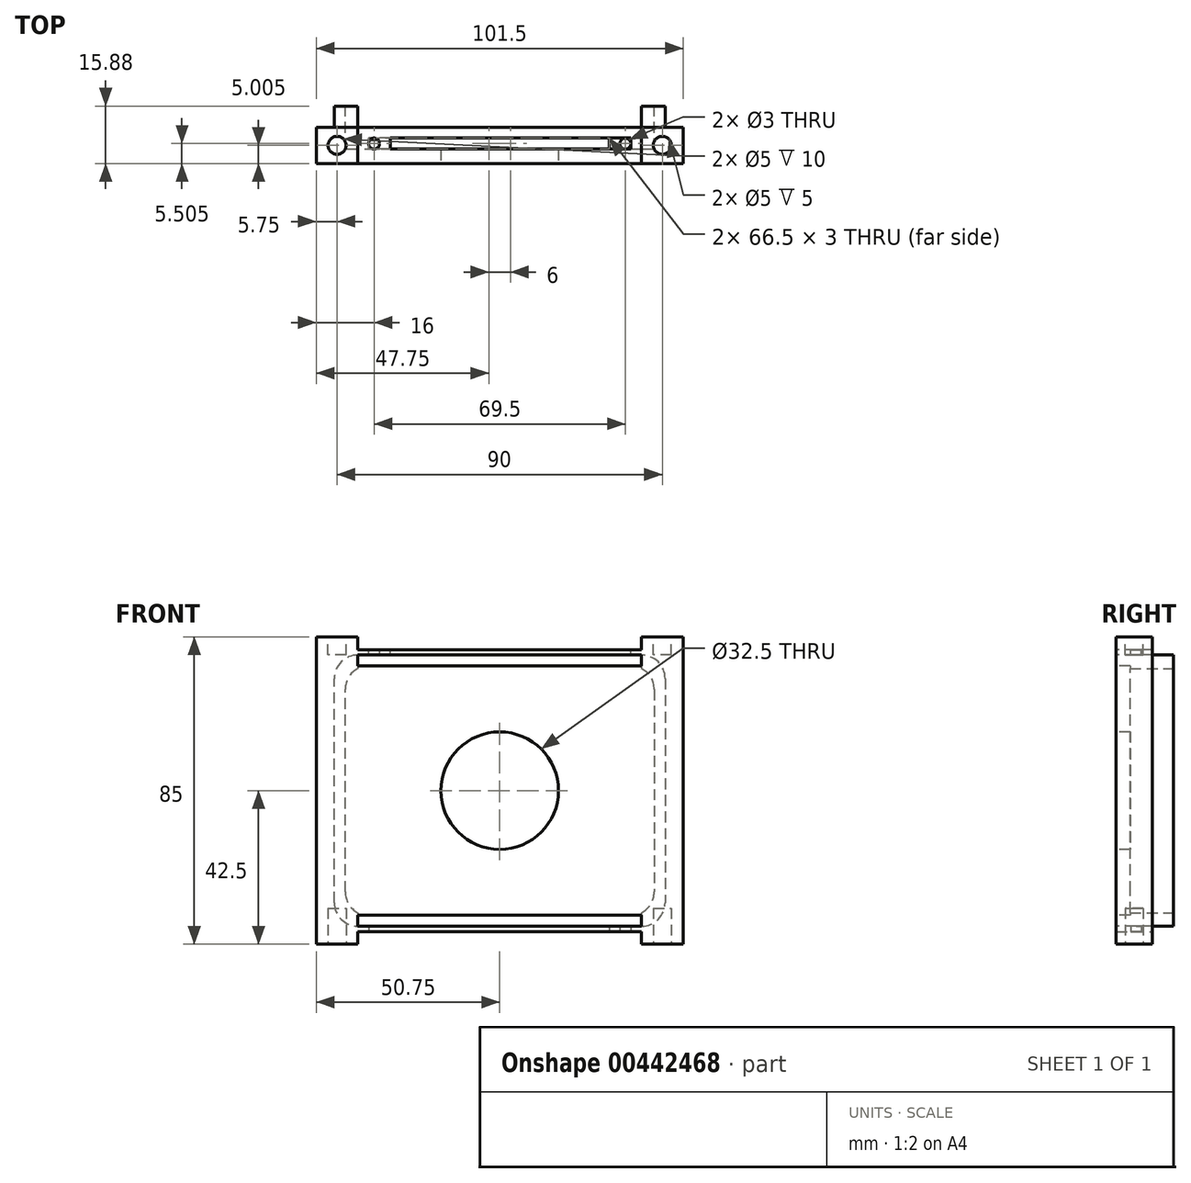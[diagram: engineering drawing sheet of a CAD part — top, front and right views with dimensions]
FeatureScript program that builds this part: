
annotation { "Feature Type Name" : "Feature", "Feature Type Description" : "" }
export const myFeature = defineFeature(function(context is Context, id is Id, definition is map)
    precondition{}
    {
        {
            var Q0;
            Q0=qCreatedBy(makeId("Front.planeOp"),FACE);
            var sketch = newSketch(context, id + "F0", { "sketchPlane" : qUnion([Q0])});
            skLineSegment(sketch, "E0.bottom", {"start": v(50.75, 42.5) * mm, "end": v(-50.75, 42.5) * mm});
            skLineSegment(sketch, "E0.top", {"start": v(50.75, -42.5) * mm, "end": v(-50.75, -42.5) * mm});
            skLineSegment(sketch, "E0.left", {"start": v(50.75, 42.5) * mm, "end": v(50.75, -42.5) * mm});
            skLineSegment(sketch, "E0.right", {"start": v(-50.75, 42.5) * mm, "end": v(-50.75, -42.5) * mm});
            skPoint(sketch, "E0.middle", {"position": v(0, 0) * mm});
            skSolve(sketch);
        }
        {
            var Q0;
            Q0 = qSketchRegion(id + "F0", true);
            extrude(context, id + "F1", {"entities" : qUnion([Q0]), "depth" : 15.88 * mm});
        }
        {
            var Q0;
            Q0=makeQuery(id+"F1.opExtrude","CAP_FACE",FACE,{"disambiguationData":[OSD([sQuery(id+"F0.wireOp",EDGE,"E0.bottom"),sQuery(id+"F0.wireOp",EDGE,"E0.top"),sQuery(id+"F0.wireOp",EDGE,"E0.left"),sQuery(id+"F0.wireOp",EDGE,"E0.right")])],"isStart":false});
            var sketch = newSketch(context, id + "F2", { "sketchPlane" : qUnion([Q0])});
            skCircle(sketch, "E1", {"center": v(0, 0) * mm, "radius": 16.25 * mm});
            skSolve(sketch);
        }
        {
            var Q0;
            Q0 = qSketchRegion(id + "F2", true);
            extrude(context, id + "F3", {"entities" : qUnion([Q0]), "operationType" : NewBodyOperationType.REMOVE, "oppositeDirection" : true, "depth" : 25 * mm});
        }
        {
            var Q0;
            Q0=makeQuery(id+"F1.opExtrude","CAP_FACE",FACE,{"disambiguationData":[OSD([sQuery(id+"F0.wireOp",EDGE,"E0.bottom"),sQuery(id+"F0.wireOp",EDGE,"E0.top"),sQuery(id+"F0.wireOp",EDGE,"E0.left"),sQuery(id+"F0.wireOp",EDGE,"E0.right")])],"isStart":true});
            var sketch = newSketch(context, id + "F4", { "sketchPlane" : qUnion([Q0])});
            skLineSegment(sketch, "E2.bottom", {"start": v(45.75, 37.5) * mm, "end": v(-45.75, 37.5) * mm, "construction": true});
            skLineSegment(sketch, "E2.top", {"start": v(45.75, -37.5) * mm, "end": v(-45.75, -37.5) * mm, "construction": true});
            skLineSegment(sketch, "E2.left", {"start": v(45.75, 37.5) * mm, "end": v(45.75, -37.5) * mm, "construction": true});
            skLineSegment(sketch, "E2.right", {"start": v(-45.75, 37.5) * mm, "end": v(-45.75, -37.5) * mm, "construction": true});
            skPoint(sketch, "E2.middle", {"position": v(0, 0) * mm});
            skCircle(sketch, "E3", {"center": v(-39.25, 31) * mm, "radius": 6.5 * mm, "construction": true});
            skCircle(sketch, "E4", {"center": v(-39.25, -31) * mm, "radius": 6.5 * mm, "construction": true});
            skCircle(sketch, "E5", {"center": v(39.25, -31) * mm, "radius": 6.5 * mm, "construction": true});
            skCircle(sketch, "E6", {"center": v(39.25, 31) * mm, "radius": 6.5 * mm, "construction": true});
            skLineSegment(sketch, "E7", {"start": v(-45.75, 31) * mm, "end": v(-45.75, -31) * mm});
            skLineSegment(sketch, "E8", {"start": v(-39.25, -37.5) * mm, "end": v(39.25, -37.5) * mm});
            skLineSegment(sketch, "E9", {"start": v(45.75, -31) * mm, "end": v(45.75, 31) * mm});
            skLineSegment(sketch, "E10", {"start": v(39.25, 37.5) * mm, "end": v(-39.25, 37.5) * mm});
            skArc(sketch, "E11", {"start": v(-39.25, 37.5) * mm, "mid": v(-43.85, 35.6) * mm, "end": v(-45.75, 31) * mm});
            skArc(sketch, "E12", {"start": v(-45.75, -31) * mm, "mid": v(-43.85, -35.6) * mm, "end": v(-39.25, -37.5) * mm});
            skArc(sketch, "E13", {"start": v(39.25, -37.5) * mm, "mid": v(43.85, -35.6) * mm, "end": v(45.75, -31) * mm});
            skArc(sketch, "E14", {"start": v(45.75, 31) * mm, "mid": v(43.85, 35.6) * mm, "end": v(39.25, 37.5) * mm});
            skLineSegment(sketch, "E15.bottom", {"start": v(50.75, 42.5) * mm, "end": v(-50.75, 42.5) * mm});
            skLineSegment(sketch, "E15.top", {"start": v(50.75, -42.5) * mm, "end": v(-50.75, -42.5) * mm});
            skLineSegment(sketch, "E15.left", {"start": v(50.75, 42.5) * mm, "end": v(50.75, -42.5) * mm});
            skLineSegment(sketch, "E15.right", {"start": v(-50.75, 42.5) * mm, "end": v(-50.75, -42.5) * mm});
            skSolve(sketch);
        }
        {
            var Q0;
            Q0 = qSketchRegion(id + "F4", true);
            extrude(context, id + "F5", {"entities" : qUnion([Q0]), "operationType" : NewBodyOperationType.REMOVE, "oppositeDirection" : true, "depth" : 5.88 * mm});
        }
        {
            var Q0;
            Q0=makeQuery(id+"F1.opExtrude","CAP_FACE",FACE,{"disambiguationData":[OSD([sQuery(id+"F0.wireOp",EDGE,"E0.bottom"),sQuery(id+"F0.wireOp",EDGE,"E0.top"),sQuery(id+"F0.wireOp",EDGE,"E0.left"),sQuery(id+"F0.wireOp",EDGE,"E0.right")])],"isStart":true});
            var sketch = newSketch(context, id + "F6", { "sketchPlane" : qUnion([Q0])});
            skLineSegment(sketch, "E16.bottom", {"start": v(42.75, 34.5) * mm, "end": v(-42.75, 34.5) * mm, "construction": true});
            skLineSegment(sketch, "E16.top", {"start": v(42.75, -34.5) * mm, "end": v(-42.75, -34.5) * mm, "construction": true});
            skLineSegment(sketch, "E16.left", {"start": v(42.75, 34.5) * mm, "end": v(42.75, -34.5) * mm, "construction": true});
            skLineSegment(sketch, "E16.right", {"start": v(-42.75, 34.5) * mm, "end": v(-42.75, -34.5) * mm, "construction": true});
            skPoint(sketch, "E16.middle", {"position": v(0, 0) * mm});
            skCircle(sketch, "E17", {"center": v(-36.25, 28) * mm, "radius": 6.5 * mm, "construction": true});
            skCircle(sketch, "E18", {"center": v(-36.25, -28) * mm, "radius": 6.5 * mm, "construction": true});
            skCircle(sketch, "E19", {"center": v(36.25, -28) * mm, "radius": 6.5 * mm, "construction": true});
            skCircle(sketch, "E20", {"center": v(36.25, 28) * mm, "radius": 6.5 * mm, "construction": true});
            skLineSegment(sketch, "E21", {"start": v(-42.75, 28) * mm, "end": v(-42.75, -28) * mm});
            skLineSegment(sketch, "E22", {"start": v(-36.25, -34.5) * mm, "end": v(36.25, -34.5) * mm});
            skLineSegment(sketch, "E23", {"start": v(42.75, -28) * mm, "end": v(42.75, 28) * mm});
            skLineSegment(sketch, "E24", {"start": v(36.25, 34.5) * mm, "end": v(-36.25, 34.5) * mm});
            skArc(sketch, "E25", {"start": v(-36.25, 34.5) * mm, "mid": v(-40.85, 32.6) * mm, "end": v(-42.75, 28) * mm});
            skArc(sketch, "E26", {"start": v(-42.75, -28) * mm, "mid": v(-40.85, -32.6) * mm, "end": v(-36.25, -34.5) * mm});
            skArc(sketch, "E27", {"start": v(36.25, -34.5) * mm, "mid": v(40.85, -32.6) * mm, "end": v(42.75, -28) * mm});
            skArc(sketch, "E28", {"start": v(42.75, 28) * mm, "mid": v(40.85, 32.6) * mm, "end": v(36.25, 34.5) * mm});
            skSolve(sketch);
        }
        {
            var Q0;
            Q0 = qSketchRegion(id + "F6", true);
            extrude(context, id + "F7", {"entities" : qUnion([Q0]), "operationType" : NewBodyOperationType.REMOVE, "oppositeDirection" : true, "depth" : 12 * mm});
        }
        {
            var Q0;
            Q0=makeQuery(id+"F1.opExtrude","SWEPT_FACE",FACE,{"disambiguationData":[OSD([sQuery(id+"F0.wireOp",EDGE,"E0.bottom")])]});
            var sketch = newSketch(context, id + "F8", { "sketchPlane" : qUnion([Q0])});
            skLineSegment(sketch, "E29.bottom", {"start": v(-39.25, -5.88) * mm, "end": v(39.25, -5.88) * mm});
            skLineSegment(sketch, "E29.top", {"start": v(-39.25, -15.88) * mm, "end": v(39.25, -15.88) * mm});
            skLineSegment(sketch, "E29.left", {"start": v(-39.25, -5.88) * mm, "end": v(-39.25, -15.88) * mm});
            skLineSegment(sketch, "E29.right", {"start": v(39.25, -5.88) * mm, "end": v(39.25, -15.88) * mm});
            skSolve(sketch);
        }
        {
            var Q0;
            Q0 = qSketchRegion(id + "F8", true);
            extrude(context, id + "F9", {"entities" : qUnion([Q0]), "operationType" : NewBodyOperationType.REMOVE, "oppositeDirection" : true, "depth" : 3.5 * mm});
        }
        {
            var Q0;
            Q0=makeQuery(id+"F1.opExtrude","SWEPT_FACE",FACE,{"disambiguationData":[OSD([sQuery(id+"F0.wireOp",EDGE,"E0.top")])]});
            var sketch = newSketch(context, id + "F10", { "sketchPlane" : qUnion([Q0])});
            skLineSegment(sketch, "E30.bottom", {"start": v(-39.25, 15.88) * mm, "end": v(39.25, 15.88) * mm});
            skLineSegment(sketch, "E30.top", {"start": v(-39.25, 5.88) * mm, "end": v(39.25, 5.88) * mm});
            skLineSegment(sketch, "E30.left", {"start": v(-39.25, 15.88) * mm, "end": v(-39.25, 5.88) * mm});
            skLineSegment(sketch, "E30.right", {"start": v(39.25, 15.88) * mm, "end": v(39.25, 5.88) * mm});
            skSolve(sketch);
        }
        {
            var Q0;
            Q0 = qSketchRegion(id + "F10", true);
            extrude(context, id + "F11", {"entities" : qUnion([Q0]), "operationType" : NewBodyOperationType.REMOVE, "oppositeDirection" : true, "depth" : 3.5 * mm});
        }
        {
            var Q0;
            Q0=makeQuery(id+"F1.opExtrude","CAP_FACE",FACE,{"disambiguationData":[OSD([sQuery(id+"F0.wireOp",EDGE,"E0.bottom"),sQuery(id+"F0.wireOp",EDGE,"E0.top"),sQuery(id+"F0.wireOp",EDGE,"E0.left"),sQuery(id+"F0.wireOp",EDGE,"E0.right")])],"isStart":false});
            var sketch = newSketch(context, id + "F12", { "sketchPlane" : qUnion([Q0])});
            skLineSegment(sketch, "E31.bottom", {"start": v(-39.25, 37.5) * mm, "end": v(39.25, 37.5) * mm});
            skLineSegment(sketch, "E31.top", {"start": v(-39.25, 34.5) * mm, "end": v(39.25, 34.5) * mm});
            skLineSegment(sketch, "E31.left", {"start": v(-39.25, 37.5) * mm, "end": v(-39.25, 34.5) * mm});
            skLineSegment(sketch, "E31.right", {"start": v(39.25, 37.5) * mm, "end": v(39.25, 34.5) * mm});
            skLineSegment(sketch, "E32.bottom", {"start": v(39.25, -37.5) * mm, "end": v(-39.25, -37.5) * mm});
            skLineSegment(sketch, "E32.top", {"start": v(39.25, -34.5) * mm, "end": v(-39.25, -34.5) * mm});
            skLineSegment(sketch, "E32.left", {"start": v(39.25, -37.5) * mm, "end": v(39.25, -34.5) * mm});
            skLineSegment(sketch, "E32.right", {"start": v(-39.25, -37.5) * mm, "end": v(-39.25, -34.5) * mm});
            skSolve(sketch);
        }
        {
            var Q0;
            Q0 = qSketchRegion(id + "F12", true);
            extrude(context, id + "F13", {"entities" : qUnion([Q0]), "operationType" : NewBodyOperationType.REMOVE, "oppositeDirection" : true, "depth" : 25 * mm});
        }
        {
            var Q0;
            Q0=makeQuery(id+"F9.boolean.opBoolean","COPY",FACE,{"derivedFrom":makeQuery(id+"F9.opExtrude","CAP_FACE",FACE,{"disambiguationData":[OSD([sQuery(id+"F8.wireOp",EDGE,"E29.bottom"),sQuery(id+"F8.wireOp",EDGE,"E29.top"),sQuery(id+"F8.wireOp",EDGE,"E29.left"),sQuery(id+"F8.wireOp",EDGE,"E29.right")])],"isStart":false})});
            var sketch = newSketch(context, id + "F14", { "sketchPlane" : qUnion([Q0])});
            skLineSegment(sketch, "E33.bottom", {"start": v(-39.25, -5.88) * mm, "end": v(39.25, -5.88) * mm});
            skLineSegment(sketch, "E33.top", {"start": v(-39.25, 11.7) * mm, "end": v(39.25, 11.7) * mm});
            skLineSegment(sketch, "E33.left", {"start": v(-39.25, -5.88) * mm, "end": v(-39.25, 11.7) * mm});
            skLineSegment(sketch, "E33.right", {"start": v(39.25, -5.88) * mm, "end": v(39.25, 11.7) * mm});
            skSolve(sketch);
        }
        {
            var Q0;
            Q0 = qSketchRegion(id + "F14", true);
            extrude(context, id + "F15", {"entities" : qUnion([Q0]), "operationType" : NewBodyOperationType.REMOVE, "oppositeDirection" : true, "depth" : 200 * mm});
        }
        {
            var Q0;
            Q0=makeQuery(id+"F5.boolean.opBoolean","COPY",FACE,{"derivedFrom":makeQuery(id+"F5.opExtrude","CAP_FACE",FACE,{"disambiguationData":[OSD([sQuery(id+"F4.wireOp",EDGE,"E7"),sQuery(id+"F4.wireOp",EDGE,"E8"),sQuery(id+"F4.wireOp",EDGE,"E9"),sQuery(id+"F4.wireOp",EDGE,"E10"),sQuery(id+"F4.wireOp",EDGE,"E11"),sQuery(id+"F4.wireOp",EDGE,"E12"),sQuery(id+"F4.wireOp",EDGE,"E13"),sQuery(id+"F4.wireOp",EDGE,"E14"),sQuery(id+"F4.wireOp",EDGE,"E15.bottom"),sQuery(id+"F4.wireOp",EDGE,"E15.top"),sQuery(id+"F4.wireOp",EDGE,"E15.left"),sQuery(id+"F4.wireOp",EDGE,"E15.right")])],"isStart":false})});
            var sketch = newSketch(context, id + "F16", { "sketchPlane" : qUnion([Q0])});
            skLineSegment(sketch, "E34.bottom", {"start": v(-39.25, 37.5) * mm, "end": v(39.25, 37.5) * mm});
            skLineSegment(sketch, "E34.top", {"start": v(-39.25, -37.5) * mm, "end": v(39.25, -37.5) * mm});
            skLineSegment(sketch, "E34.left", {"start": v(-39.25, 37.5) * mm, "end": v(-39.25, -37.5) * mm});
            skLineSegment(sketch, "E34.right", {"start": v(39.25, 37.5) * mm, "end": v(39.25, -37.5) * mm});
            skSolve(sketch);
        }
        {
            var Q0;
            Q0 = qSketchRegion(id + "F16", true);
            extrude(context, id + "F17", {"entities" : qUnion([Q0]), "operationType" : NewBodyOperationType.REMOVE, "oppositeDirection" : true, "depth" : 6.12 * mm});
        }
        {
            var Q0;
            Q0=makeQuery(id+"F9.boolean.opBoolean","COPY",FACE,{"derivedFrom":makeQuery(id+"F9.opExtrude","CAP_FACE",FACE,{"disambiguationData":[OSD([sQuery(id+"F8.wireOp",EDGE,"E29.bottom"),sQuery(id+"F8.wireOp",EDGE,"E29.top"),sQuery(id+"F8.wireOp",EDGE,"E29.left"),sQuery(id+"F8.wireOp",EDGE,"E29.right")])],"isStart":false})});
            var sketch = newSketch(context, id + "F18", { "sketchPlane" : qUnion([Q0])});
            skCircle(sketch, "E35", {"center": v(-34.75, -10.38) * mm, "radius": 1.5 * mm});
            skLineSegment(sketch, "E36.bottom", {"start": v(-30.25, -8.88) * mm, "end": v(36.25, -8.87) * mm});
            skLineSegment(sketch, "E36.top", {"start": v(-30.25, -11.88) * mm, "end": v(36.25, -11.87) * mm});
            skLineSegment(sketch, "E36.left", {"start": v(-30.25, -8.88) * mm, "end": v(-30.25, -11.88) * mm});
            skLineSegment(sketch, "E36.right", {"start": v(36.25, -8.87) * mm, "end": v(36.25, -11.87) * mm});
            skSolve(sketch);
        }
        {
            var Q0;
            Q0 = qSketchRegion(id + "F18", true);
            extrude(context, id + "F19", {"entities" : qUnion([Q0]), "operationType" : NewBodyOperationType.REMOVE, "oppositeDirection" : true, "depth" : 2 * mm});
        }
        {
            var Q0;
            Q0=makeQuery(id+"F11.boolean.opBoolean","COPY",FACE,{"derivedFrom":makeQuery(id+"F11.opExtrude","CAP_FACE",FACE,{"disambiguationData":[OSD([sQuery(id+"F10.wireOp",EDGE,"E30.bottom"),sQuery(id+"F10.wireOp",EDGE,"E30.top"),sQuery(id+"F10.wireOp",EDGE,"E30.left"),sQuery(id+"F10.wireOp",EDGE,"E30.right")])],"isStart":false})});
            var sketch = newSketch(context, id + "F20", { "sketchPlane" : qUnion([Q0])});
            skCircle(sketch, "E37", {"center": v(34.75, 10.38) * mm, "radius": 1.5 * mm});
            skLineSegment(sketch, "E38.bottom", {"start": v(-36.25, 11.87) * mm, "end": v(30.25, 11.88) * mm});
            skLineSegment(sketch, "E38.top", {"start": v(-36.25, 8.87) * mm, "end": v(30.25, 8.88) * mm});
            skLineSegment(sketch, "E38.left", {"start": v(-36.25, 11.88) * mm, "end": v(-36.25, 8.87) * mm});
            skLineSegment(sketch, "E38.right", {"start": v(30.25, 11.88) * mm, "end": v(30.25, 8.88) * mm});
            skSolve(sketch);
        }
        {
            var Q0;
            Q0 = qSketchRegion(id + "F20", true);
            extrude(context, id + "F21", {"entities" : qUnion([Q0]), "operationType" : NewBodyOperationType.REMOVE, "oppositeDirection" : true, "depth" : 2 * mm});
        }
        {
            var Q0;
            {var subQ0=sQuery(id+"F0.wireOp",EDGE,"E0.right");var subQ1=sQuery(id+"F0.wireOp",EDGE,"E0.top");Q0=makeQuery(id+"F11.boolean.opBoolean","SPLIT",FACE,{"disambiguationData":[TD([makeQuery(id+"F1.opExtrude","SWEPT_FACE",FACE,{"disambiguationData":[OSD([subQ0])]})])],"derivedFrom":makeQuery(id+"F1.opExtrude","SWEPT_FACE",FACE,{"disambiguationData":[OSD([subQ1])]})});}
            var sketch = newSketch(context, id + "F22", { "sketchPlane" : qUnion([Q0])});
            skLineSegment(sketch, "E39", {"start": v(-50.75, 15.87) * mm, "end": v(-39.25, 5.87) * mm, "construction": true});
            skLineSegment(sketch, "E40", {"start": v(-39.25, 5.88) * mm, "end": v(50.77, 5.88) * mm, "construction": true});
            skLineSegment(sketch, "E41", {"start": v(50.77, 5.87) * mm, "end": v(66.59, 13.67) * mm, "construction": true});
            skLineSegment(sketch, "E42", {"start": v(66.59, 13.67) * mm, "end": v(61.79, 23.42) * mm, "construction": true});
            skLineSegment(sketch, "E43", {"start": v(-39.25, 15.88) * mm, "end": v(-50.75, 5.88) * mm, "construction": true});
            skCircle(sketch, "E44", {"center": v(-45, 10.87) * mm, "radius": 2.5 * mm});
            skSolve(sketch);
        }
        {
            var Q0;
            Q0 = qSketchRegion(id + "F22", true);
            extrude(context, id + "F23", {"entities" : qUnion([Q0]), "operationType" : NewBodyOperationType.REMOVE, "oppositeDirection" : true, "depth" : 10 * mm});
        }
        {
            var Q0;
            {var subQ0=sQuery(id+"F0.wireOp",EDGE,"E0.left");var subQ1=sQuery(id+"F0.wireOp",EDGE,"E0.top");Q0=makeQuery(id+"F11.boolean.opBoolean","SPLIT",FACE,{"disambiguationData":[TD([makeQuery(id+"F1.opExtrude","SWEPT_FACE",FACE,{"disambiguationData":[OSD([subQ0])]})])],"derivedFrom":makeQuery(id+"F1.opExtrude","SWEPT_FACE",FACE,{"disambiguationData":[OSD([subQ1])]})});}
            var sketch = newSketch(context, id + "F24", { "sketchPlane" : qUnion([Q0])});
            skLineSegment(sketch, "E45", {"start": v(39.25, 15.88) * mm, "end": v(50.75, 5.88) * mm, "construction": true});
            skLineSegment(sketch, "E46", {"start": v(50.75, 5.88) * mm, "end": v(50.75, 15.88) * mm, "construction": true});
            skLineSegment(sketch, "E47", {"start": v(50.75, 15.88) * mm, "end": v(39.25, 5.88) * mm, "construction": true});
            skCircle(sketch, "E48", {"center": v(45, 10.88) * mm, "radius": 2.5 * mm});
            skSolve(sketch);
        }
        {
            var Q0;
            Q0 = qSketchRegion(id + "F24", true);
            extrude(context, id + "F25", {"entities" : qUnion([Q0]), "operationType" : NewBodyOperationType.REMOVE, "oppositeDirection" : true, "depth" : 10 * mm});
        }
        {
            var Q0;
            {var subQ0=sQuery(id+"F0.wireOp",EDGE,"E0.right");var subQ1=sQuery(id+"F0.wireOp",EDGE,"E0.bottom");Q0=makeQuery(id+"F9.boolean.opBoolean","SPLIT",FACE,{"disambiguationData":[TD([makeQuery(id+"F1.opExtrude","SWEPT_FACE",FACE,{"disambiguationData":[OSD([subQ0])]})])],"derivedFrom":makeQuery(id+"F1.opExtrude","SWEPT_FACE",FACE,{"disambiguationData":[OSD([subQ1])]})});}
            var sketch = newSketch(context, id + "F26", { "sketchPlane" : qUnion([Q0])});
            skLineSegment(sketch, "E49", {"start": v(-50.75, -5.88) * mm, "end": v(-39.25, -15.88) * mm, "construction": true});
            skLineSegment(sketch, "E50", {"start": v(-39.25, -15.88) * mm, "end": v(-39.25, -5.88) * mm, "construction": true});
            skLineSegment(sketch, "E51", {"start": v(-39.25, -5.88) * mm, "end": v(-50.75, -15.88) * mm, "construction": true});
            skCircle(sketch, "E52", {"center": v(-45, -10.88) * mm, "radius": 2.5 * mm});
            skSolve(sketch);
        }
        {
            var Q0;
            Q0 = qSketchRegion(id + "F26", true);
            extrude(context, id + "F27", {"entities" : qUnion([Q0]), "operationType" : NewBodyOperationType.REMOVE, "oppositeDirection" : true, "depth" : 5 * mm});
        }
        {
            var Q0;
            {var subQ0=sQuery(id+"F0.wireOp",EDGE,"E0.left");var subQ1=sQuery(id+"F0.wireOp",EDGE,"E0.bottom");Q0=makeQuery(id+"F9.boolean.opBoolean","SPLIT",FACE,{"disambiguationData":[TD([makeQuery(id+"F1.opExtrude","SWEPT_FACE",FACE,{"disambiguationData":[OSD([subQ0])]})])],"derivedFrom":makeQuery(id+"F1.opExtrude","SWEPT_FACE",FACE,{"disambiguationData":[OSD([subQ1])]})});}
            var sketch = newSketch(context, id + "F28", { "sketchPlane" : qUnion([Q0])});
            skLineSegment(sketch, "E53", {"start": v(50.75, -5.87) * mm, "end": v(39.25, -15.87) * mm, "construction": true});
            skLineSegment(sketch, "E54", {"start": v(39.25, -15.87) * mm, "end": v(39.25, -5.88) * mm, "construction": true});
            skLineSegment(sketch, "E55", {"start": v(39.25, -5.88) * mm, "end": v(50.75, -15.88) * mm, "construction": true});
            skCircle(sketch, "E56", {"center": v(45, -10.88) * mm, "radius": 2.5 * mm});
            skSolve(sketch);
        }
        {
            var Q0;
            Q0 = qSketchRegion(id + "F28", true);
            extrude(context, id + "F29", {"entities" : qUnion([Q0]), "operationType" : NewBodyOperationType.REMOVE, "oppositeDirection" : true, "depth" : 5 * mm});
        }
    });
